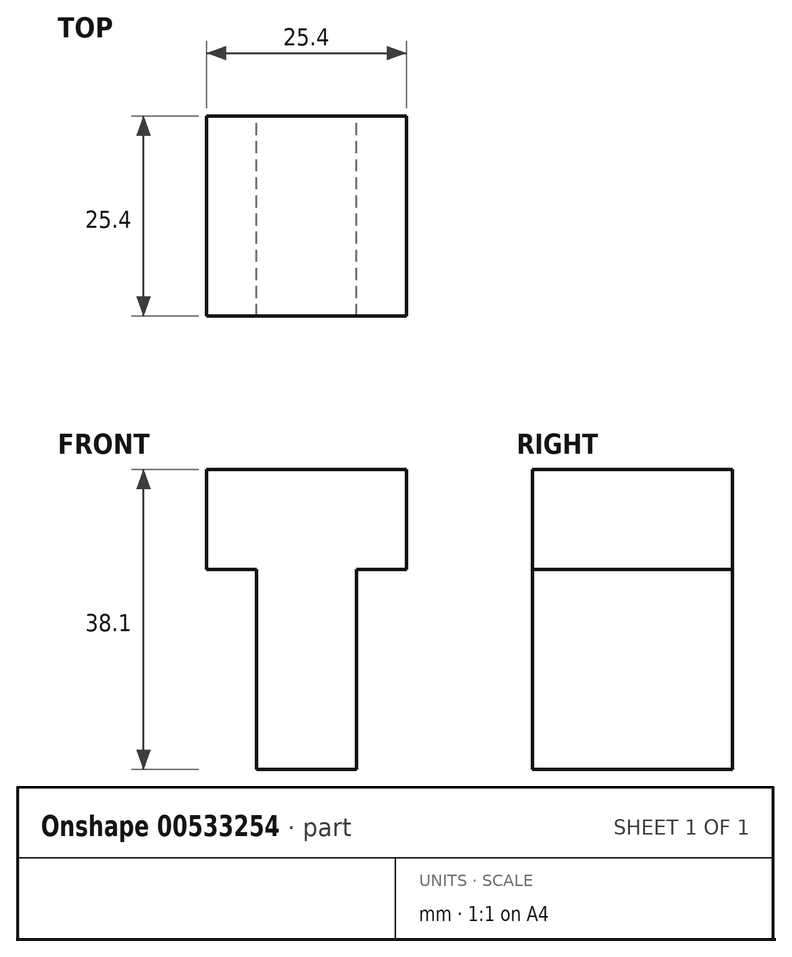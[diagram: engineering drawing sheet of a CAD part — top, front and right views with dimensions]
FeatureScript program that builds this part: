
annotation { "Feature Type Name" : "Feature", "Feature Type Description" : "" }
export const myFeature = defineFeature(function(context is Context, id is Id, definition is map)
    precondition{}
    {
        {
            var Q0;
            Q0=qCreatedBy(makeId("Front.planeOp"),FACE);
            var sketch = newSketch(context, id + "F0", { "sketchPlane" : qUnion([Q0])});
            skLineSegment(sketch, "E0", {"start": v(-53.2, 25.4) * mm, "end": v(-53.2, 0) * mm});
            skLineSegment(sketch, "E1", {"start": v(-53.2, 0) * mm, "end": v(-40.5, 0) * mm});
            skLineSegment(sketch, "E2", {"start": v(-40.5, 0) * mm, "end": v(-40.5, 25.4) * mm});
            skLineSegment(sketch, "E3", {"start": v(-40.5, 25.4) * mm, "end": v(-34.16, 25.4) * mm});
            skLineSegment(sketch, "E4", {"start": v(-53.2, 25.4) * mm, "end": v(-59.56, 25.4) * mm});
            skLineSegment(sketch, "E5", {"start": v(-59.56, 25.4) * mm, "end": v(-59.56, 38.1) * mm});
            skLineSegment(sketch, "E6", {"start": v(-34.16, 25.4) * mm, "end": v(-34.16, 38.1) * mm});
            skLineSegment(sketch, "E7", {"start": v(-59.56, 38.1) * mm, "end": v(-34.16, 38.1) * mm});
            skSolve(sketch);
        }
        {
            var Q0;
            Q0=makeQuery(id+"F0.imprint","IMPRINT",FACE,{"disambiguationData":[TD([[makeQuery(id+"F0.imprint","IMPRINT",EDGE,{"derivedFrom":sQuery(id+"F0.wireOp",EDGE,"E0")}),1.0]])]});
            extrude(context, id + "F1", {"entities" : qUnion([Q0]), "depth" : 25.4 * mm, "offsetDistance" : 25.4 * mm});
        }
    });
